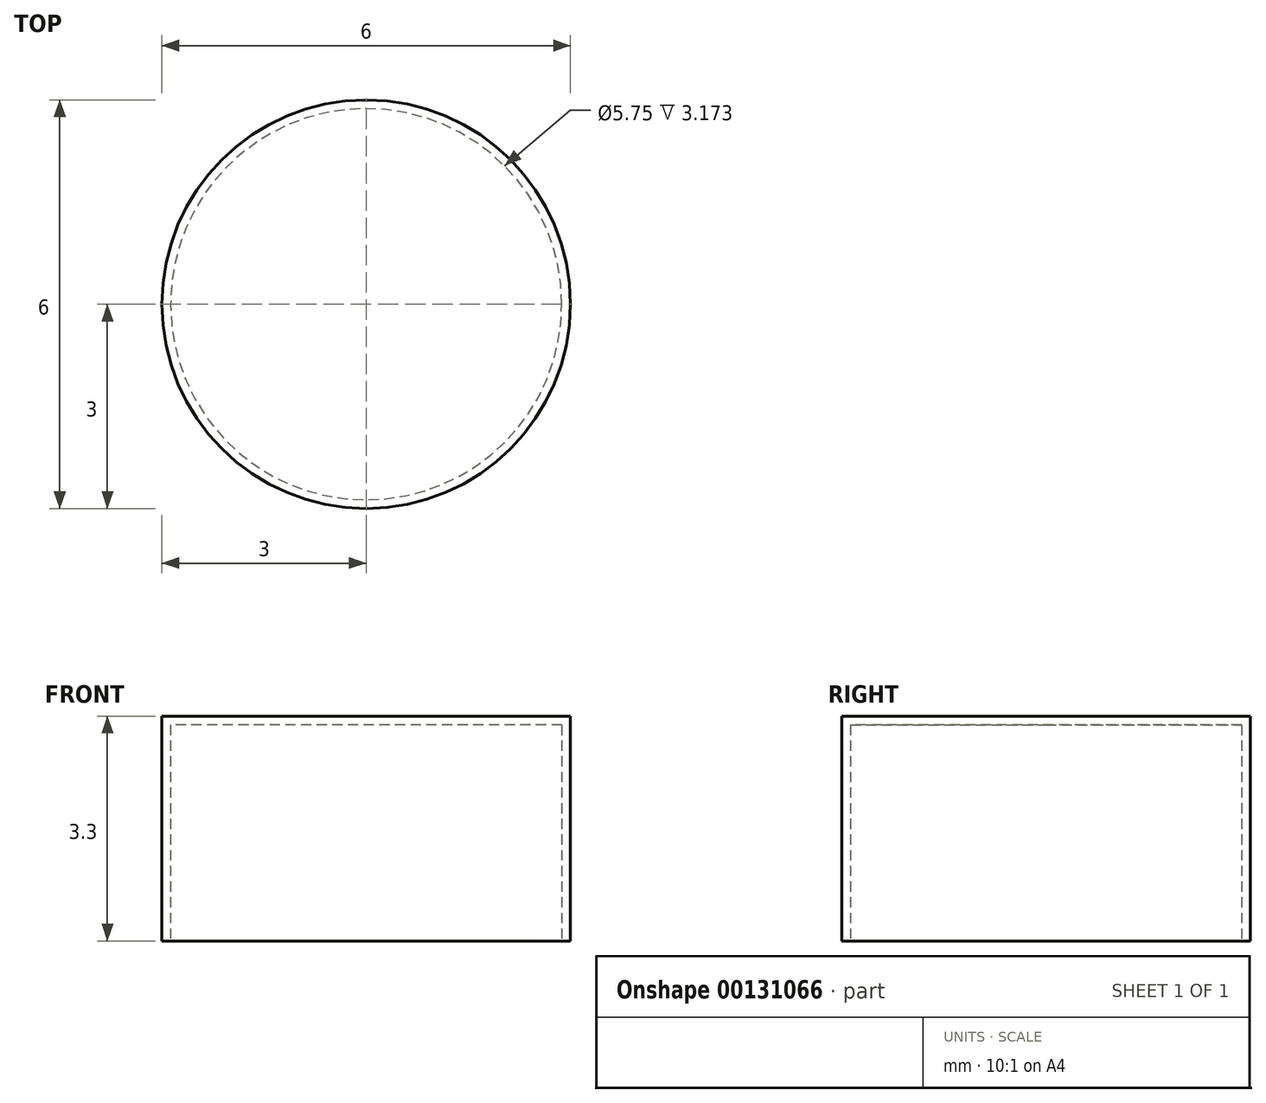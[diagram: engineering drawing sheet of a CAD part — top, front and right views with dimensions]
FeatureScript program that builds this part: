
annotation { "Feature Type Name" : "Feature", "Feature Type Description" : "" }
export const myFeature = defineFeature(function(context is Context, id is Id, definition is map)
    precondition{}
    {
        {
            var Q0;
            Q0=qCreatedBy(makeId("Top.planeOp"),FACE);
            var sketch = newSketch(context, id + "F0", { "sketchPlane" : qUnion([Q0])});
            skCircle(sketch, "E0", {"center": v(0, 0) * mm, "radius": 3 * mm});
            skSolve(sketch);
        }
        {
            var Q0;
            Q0 = qSketchRegion(id + "F0", true);
            extrude(context, id + "F1", {"entities" : qUnion([Q0]), "depth" : 3.3 * mm});
        }
        {
            var Q0;
            Q0=makeQuery(id+"F1.opExtrude","CAP_FACE",FACE,{"disambiguationData":[OSD([sQuery(id+"F0.wireOp",EDGE,"E0")])],"isStart":true});
            shell(context, id + "F2", {"entities" : qUnion([Q0]), "thickness" : 0.13 * mm});
        }
    });
